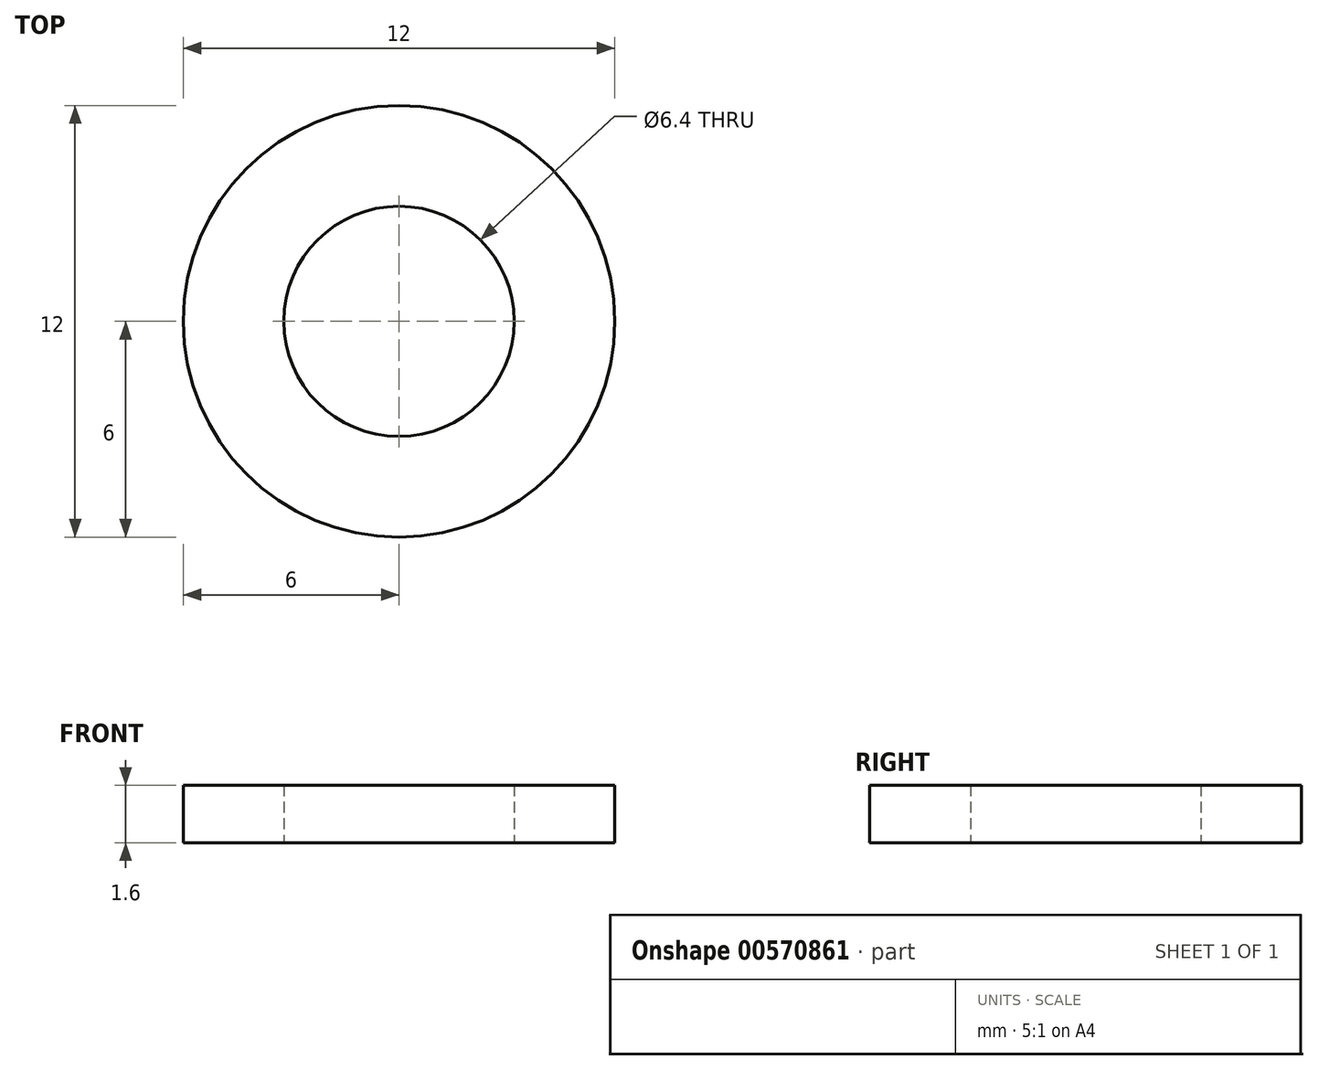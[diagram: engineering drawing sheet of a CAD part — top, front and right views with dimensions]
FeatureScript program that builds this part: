
annotation { "Feature Type Name" : "Feature", "Feature Type Description" : "" }
export const myFeature = defineFeature(function(context is Context, id is Id, definition is map)
    precondition{}
    {
        {
            var Q0;
            Q0=qCreatedBy(makeId("Top.planeOp"),FACE);
            var sketch = newSketch(context, id + "F0", { "sketchPlane" : qUnion([Q0])});
            skCircle(sketch, "E0", {"center": v(0, 0) * mm, "radius": 6 * mm});
            skCircle(sketch, "E1", {"center": v(0, 0) * mm, "radius": 3.2 * mm});
            skSolve(sketch);
        }
        {
            var Q0;
            Q0=makeQuery(id+"F0.imprint","IMPRINT",FACE,{"disambiguationData":[TD([[makeQuery(id+"F0.imprint","IMPRINT",EDGE,{"derivedFrom":sQuery(id+"F0.wireOp",EDGE,"E0")}),1.0]])]});
            extrude(context, id + "F1", {"entities" : qUnion([Q0]), "depth" : 1.6 * mm, "offsetDistance" : 25 * mm, "symmetric" : true});
        }
    });
